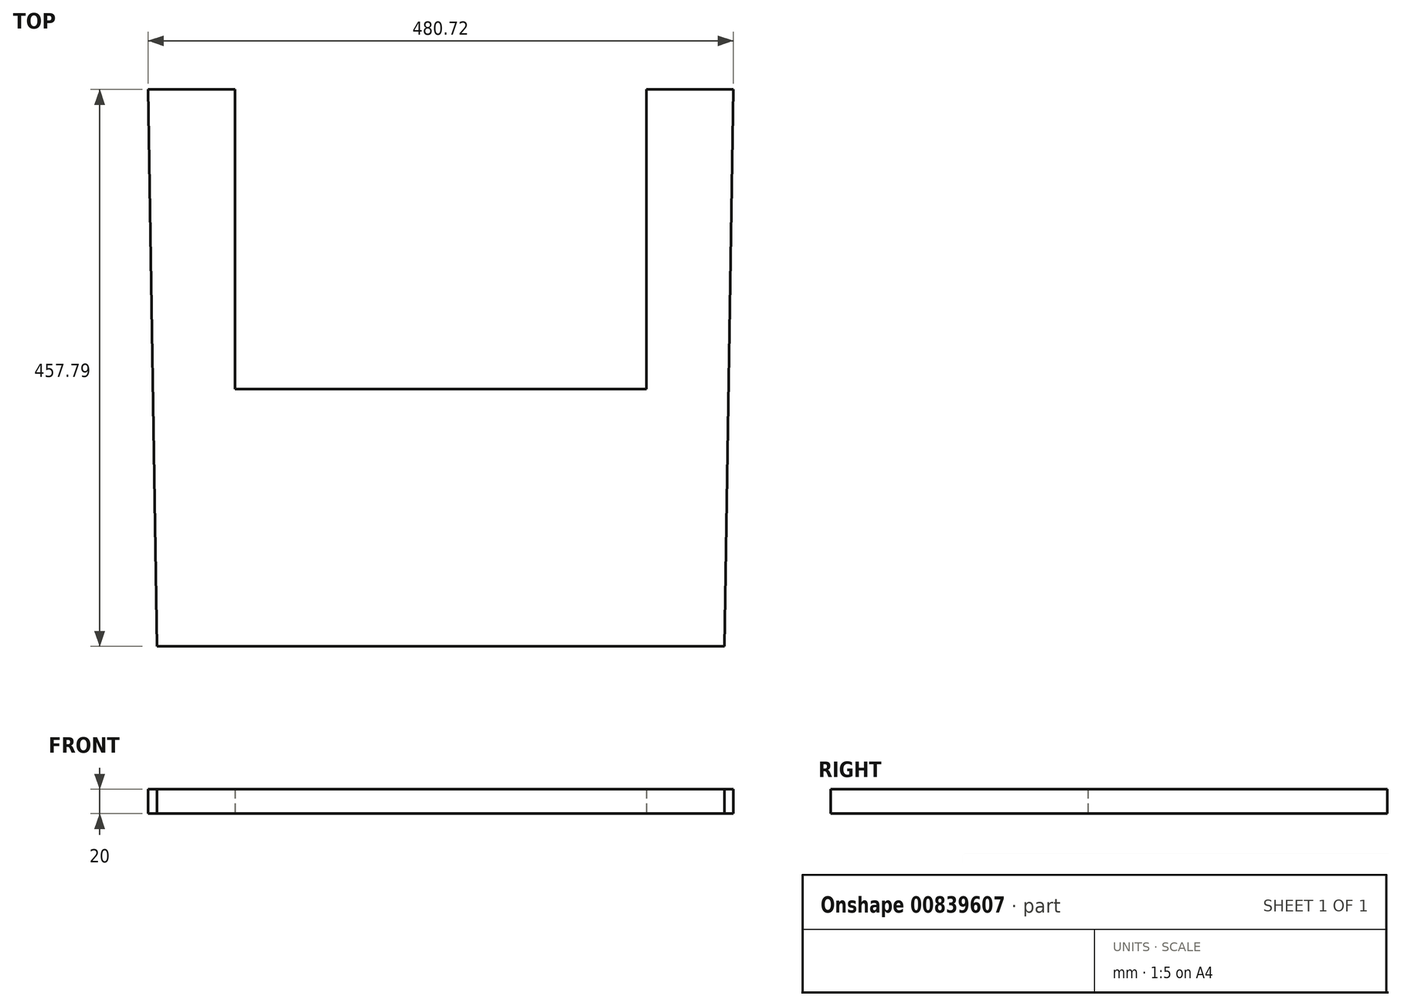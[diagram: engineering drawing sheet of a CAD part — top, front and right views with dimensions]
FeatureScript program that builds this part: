
annotation { "Feature Type Name" : "Feature", "Feature Type Description" : "" }
export const myFeature = defineFeature(function(context is Context, id is Id, definition is map)
    precondition{}
    {
        {
            var Q0;
            Q0=qCreatedBy(makeId("Top.planeOp"),FACE);
            var sketch = newSketch(context, id + "F0", { "sketchPlane" : qUnion([Q0])});
            skLineSegment(sketch, "E0", {"start": v(0, 0) * mm, "end": v(-169.03, 0) * mm, "construction": true});
            skLineSegment(sketch, "E1", {"start": v(-233.15, 88.58) * mm, "end": v(0, 88.58) * mm, "construction": true});
            skLineSegment(sketch, "E2", {"start": v(0, 88.58) * mm, "end": v(0, 300.23) * mm});
            skLineSegment(sketch, "E3", {"start": v(0, 300.23) * mm, "end": v(-169.03, 300.23) * mm});
            skLineSegment(sketch, "E4", {"start": v(-169.03, 300.23) * mm, "end": v(-169.03, 546.37) * mm});
            skLineSegment(sketch, "E5", {"start": v(-169.03, 546.37) * mm, "end": v(-240.36, 546.37) * mm});
            skLineSegment(sketch, "E6", {"start": v(-240.36, 546.37) * mm, "end": v(-233.15, 88.58) * mm});
            skLineSegment(sketch, "E7", {"start": v(-233.15, 88.58) * mm, "end": v(0, 88.58) * mm});
            skSolve(sketch);
        }
        {
            var Q0;
            Q0=makeQuery(id+"F0.imprint","IMPRINT",FACE,{"disambiguationData":[TD([[makeQuery(id+"F0.imprint","IMPRINT",EDGE,{"derivedFrom":sQuery(id+"F0.wireOp",EDGE,"E2")}),1.0]])]});
            extrude(context, id + "F1", {"entities" : qUnion([Q0]), "depth" : 20 * mm, "offsetDistance" : 25 * mm});
        }
        {
            var Q0;
            Q0=makeQuery(id+"F1.opExtrude","SWEPT_BODY",BODY,{"disambiguationData":[OSD([sQuery(id+"F0.wireOp",EDGE,"E2"),sQuery(id+"F0.wireOp",EDGE,"E3"),sQuery(id+"F0.wireOp",EDGE,"E4"),sQuery(id+"F0.wireOp",EDGE,"E5"),sQuery(id+"F0.wireOp",EDGE,"E6"),sQuery(id+"F0.wireOp",EDGE,"5boBlJdt-WujW-6EAE-54oG-6OM0BIvT9yLD"),sQuery(id+"F0.wireOp",EDGE,"mAsveMtl-i8ys-mmys-lsb6-m7JwEwHX0v6k"),sQuery(id+"F0.wireOp",EDGE,"E7")])]});
            var Q1;
            Q1=qCreatedBy(makeId("Right.planeOp"),FACE);
            mirror(context, id + "F2", {"operationType" : NewBodyOperationType.ADD, "entities" : qUnion([Q0]), "mirrorPlane" : qUnion([Q1])});
        }
    });
